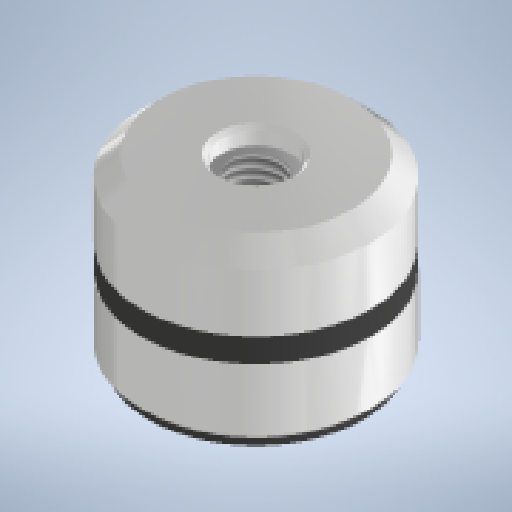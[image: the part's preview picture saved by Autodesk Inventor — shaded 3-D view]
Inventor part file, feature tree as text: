
AUTODESK INVENTOR PART (.ipt)
format: ipt  version: 2024 (Build 280153000, 153)  size: 451,072 bytes
history: native  units: mm
features: sketch x6, other x4, chamfer x4, revolve x3, hole x2, extrude x2, plane x1, fillet x1, projected_geometry x1
ambient origin geometry x8: Origin, YZ Plane, XZ Plane, XY Plane, X Axis, Y Axis, Z Axis, Center Point
bodies: Body1 (feature_tree), Body2 (feature_tree), Body3 (feature_tree), Body4 (feature_tree)
feature tree (24):
  other  "Mount"
  sketch  "Sketch1"  dims[d0=15.0mm d1=10.0mm]
  revolve  "Revolution1"  [1 undecoded]
  revolve  "Revolution2"  [1 undecoded]
  revolve  "Revolution3"  [1 undecoded]
  hole  "Hole1"  [1 undecoded]
  chamfer  "Chamfer1"  Distance=1.0mm
  plane  "Work Plane1"
  extrude  "Extrusion1"  Depth=15.0mm
  fillet  "Fillet3"  [1 undecoded]
  sketch  "Sketch4"  dims[d8=3.0mm d9=5.0mm]
  extrude  "Extrusion2"  TaperAngle=360.0deg  [1 undecoded]
  hole  "Hole2"  [1 undecoded]
  chamfer  "Chamfer2"  Distance=2.0mm Angle=45.0deg
  chamfer  "Chamfer3"  [1 undecoded]
  chamfer  "Chamfer4"  Distance=24.0mm
  other  "Damper and Pad"
  other  "Cap"
  sketch  "Sketch2"  dims[d2=105.0deg d3=18.0mm]
  sketch  "Sketch3"  dims[d4=6.0mm d6=3.0mm]
  sketch  "Sketch5"  dims[d10=1.0mm]
  other  "Leveling Nut"
  sketch  "Sketch6"  dims[d11=2.0mm d12=1.0mm d13=15.0mm d14=360.0deg d25=360.0deg d26=360.0deg d29=9.0mm d30=16.0mm d31=4.0mm d32=2.0mm d33=90.0deg d34=8.0mm d35=20.594885mm d36=2.0mm d37=2.0mm d38=45.0deg d39=-5.5mm d40=24.0mm d41=8.0mm d42=60.0mm d44=360.0deg d46=6.6mm d47=0.0mm d48=1.0mm d49=0.3mm d50=6.35mm d51=0.0mm d52=6.647mm d53=16.0mm d54=4.0mm d55=2.0mm d56=90.0deg d57=8.0mm d58=20.594885mm d59=0.5mm d60=2.0mm d61=45.0deg d64=0.75mm d65=2.0mm d66=45.0deg d67=2.5mm d68=2.0mm d69=45.0deg]
  projected_geometry  "Project Cut Edges1"
note: 8 required parameter values undecoded (feature->parameter linkage not recoverable at this tier; creation-order binding heuristic only, values carry confidence <= 0.55)